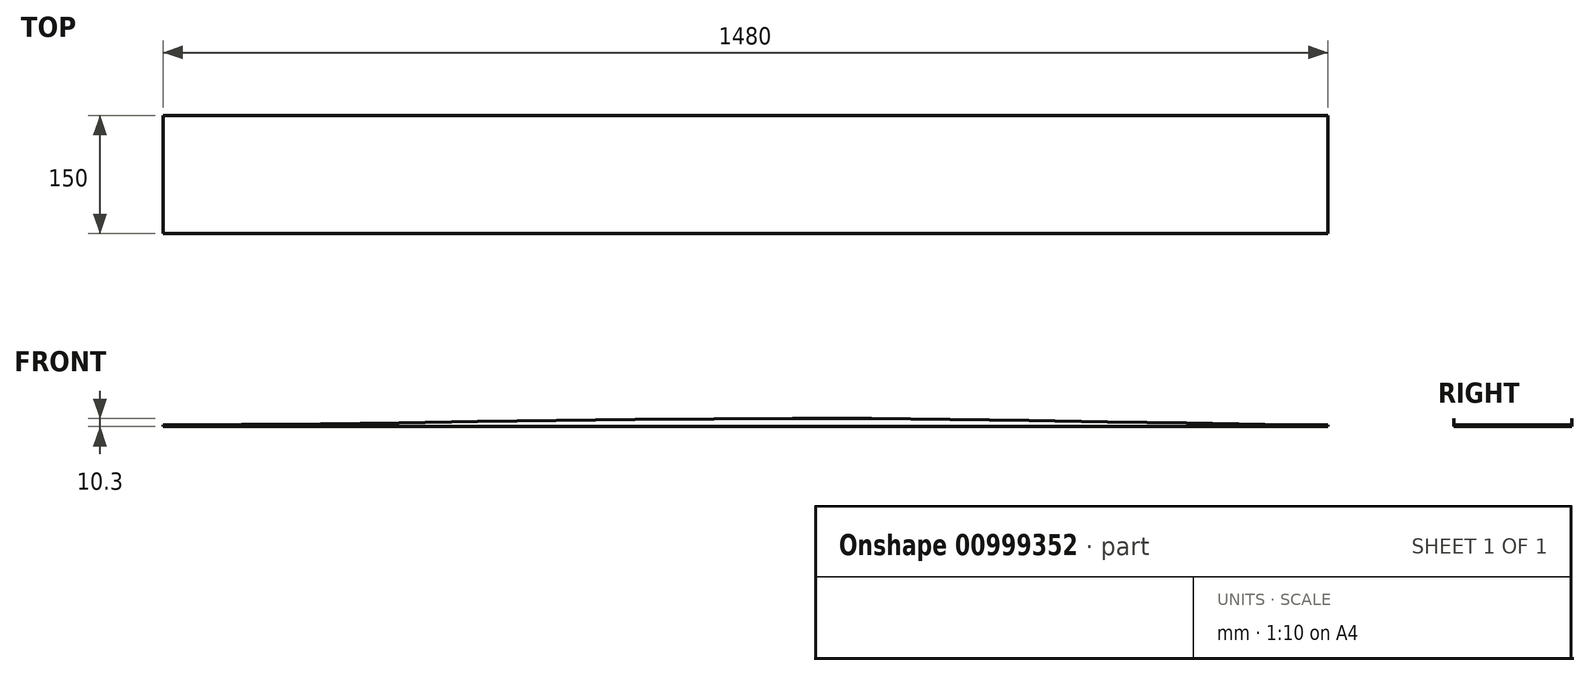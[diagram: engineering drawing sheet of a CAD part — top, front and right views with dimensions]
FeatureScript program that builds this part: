
annotation { "Feature Type Name" : "Feature", "Feature Type Description" : "" }
export const myFeature = defineFeature(function(context is Context, id is Id, definition is map)
    precondition{}
    {
        {
            var Q0;
            Q0=qCreatedBy(makeId("Front.planeOp"),FACE);
            var sketch = newSketch(context, id + "F0", { "sketchPlane" : qUnion([Q0])});
            skLineSegment(sketch, "E0", {"start": v(-740, -5.15) * mm, "end": v(-740, -3.2) * mm});
            skLineSegment(sketch, "E1", {"start": v(-740, -3.2) * mm, "end": v(-640, -2.52) * mm});
            skLineSegment(sketch, "E2", {"start": v(-640, -2.52) * mm, "end": v(-540, -1.56) * mm});
            skLineSegment(sketch, "E3", {"start": v(-540, -1.56) * mm, "end": v(-440, -0.3) * mm});
            skLineSegment(sketch, "E4", {"start": v(-440, -0.3) * mm, "end": v(-340, 1.15) * mm});
            skLineSegment(sketch, "E5", {"start": v(-340, 1.15) * mm, "end": v(-140, 3.8) * mm});
            skLineSegment(sketch, "E6", {"start": v(-140, 3.8) * mm, "end": v(-40, 4.8) * mm});
            skLineSegment(sketch, "E7", {"start": v(-40, 4.8) * mm, "end": v(60, 5.15) * mm});
            skLineSegment(sketch, "E8", {"start": v(60, 5.15) * mm, "end": v(160, 4.95) * mm});
            skLineSegment(sketch, "E9", {"start": v(160, 4.95) * mm, "end": v(260, 3.85) * mm});
            skLineSegment(sketch, "E10", {"start": v(260, 3.85) * mm, "end": v(360, 2.4) * mm});
            skLineSegment(sketch, "E11", {"start": v(360, 2.4) * mm, "end": v(460, 0.85) * mm});
            skLineSegment(sketch, "E12", {"start": v(460, 0.85) * mm, "end": v(560, -0.75) * mm});
            skLineSegment(sketch, "E13", {"start": v(560, -0.75) * mm, "end": v(660, -2.45) * mm});
            skLineSegment(sketch, "E14", {"start": v(660, -2.45) * mm, "end": v(740, -3.15) * mm});
            skLineSegment(sketch, "E15", {"start": v(740, -3.15) * mm, "end": v(740, -5.15) * mm});
            skLineSegment(sketch, "E16", {"start": v(740, -5.15) * mm, "end": v(-740, -5.15) * mm});
            skSolve(sketch);
        }
        {
            var Q0;
            Q0 = qSketchRegion(id + "F0", true);
            extrude(context, id + "F1", {"entities" : qUnion([Q0]), "depth" : 150 * mm, "offsetDistance" : 25 * mm});
        }
    });
